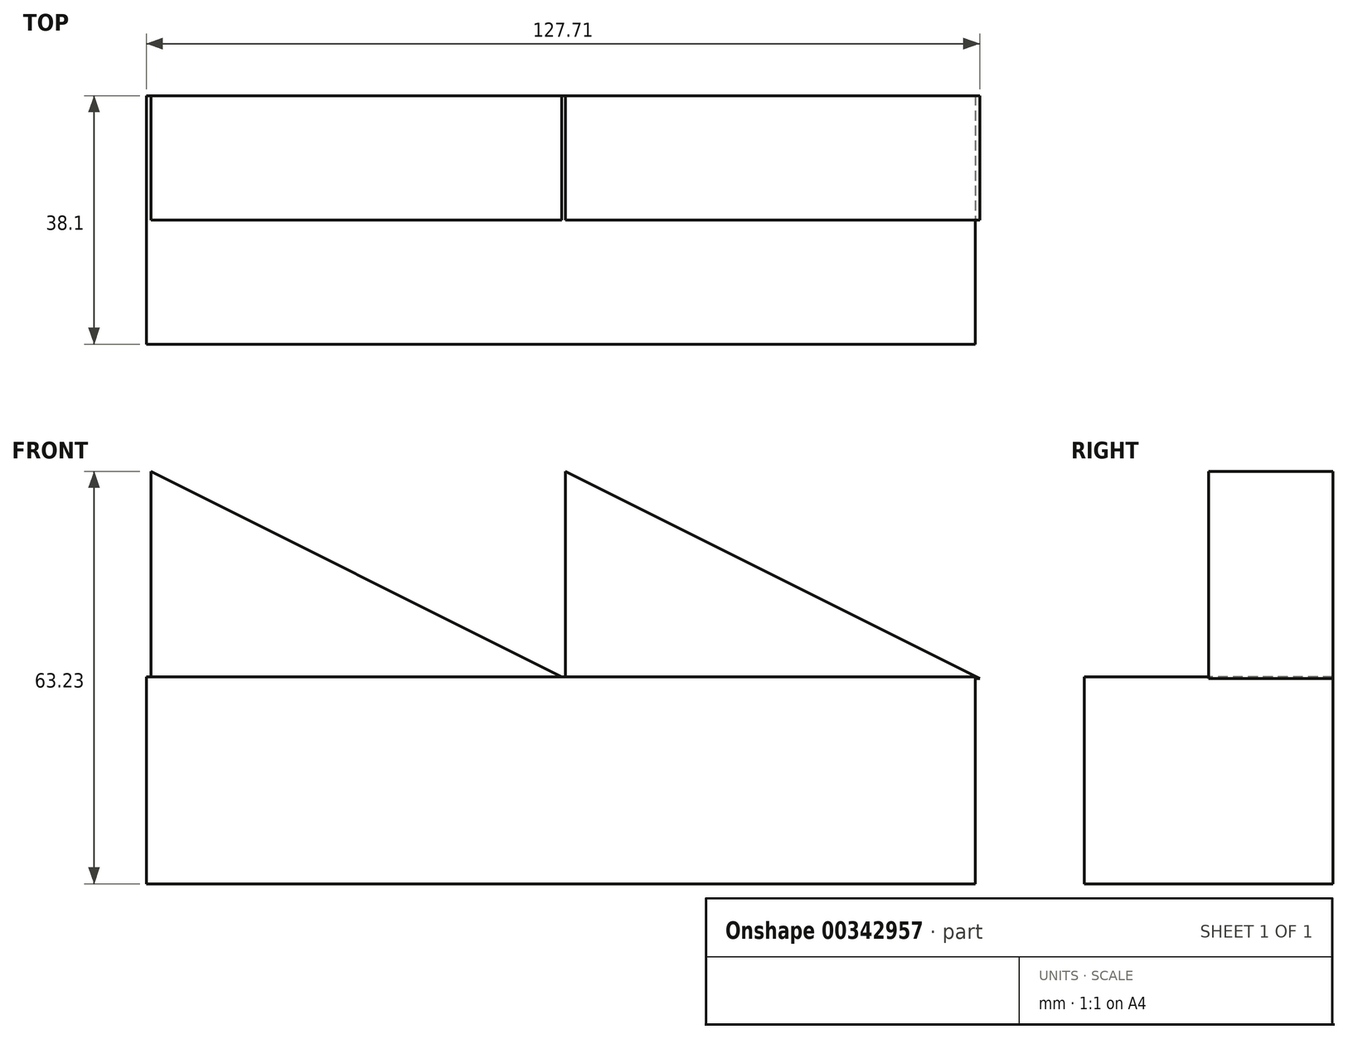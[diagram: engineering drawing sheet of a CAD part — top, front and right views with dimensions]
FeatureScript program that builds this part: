
annotation { "Feature Type Name" : "Feature", "Feature Type Description" : "" }
export const myFeature = defineFeature(function(context is Context, id is Id, definition is map)
    precondition{}
    {
        {
            var Q0;
            Q0=qCreatedBy(makeId("Front.planeOp"),FACE);
            var sketch = newSketch(context, id + "F0", { "sketchPlane" : qUnion([Q0])});
            skLineSegment(sketch, "E0", {"start": v(-53.15, -40.08) * mm, "end": v(73.85, -40.08) * mm});
            skLineSegment(sketch, "E1", {"start": v(-53.15, -40.08) * mm, "end": v(-53.15, -8.33) * mm});
            skLineSegment(sketch, "E2", {"start": v(-53.15, -8.33) * mm, "end": v(73.85, -8.33) * mm});
            skLineSegment(sketch, "E3", {"start": v(73.85, -8.33) * mm, "end": v(73.85, -40.08) * mm});
            skSolve(sketch);
        }
        {
            var Q0;
            Q0=makeQuery(id+"F0.imprint","IMPRINT",FACE,{"disambiguationData":[TD([[makeQuery(id+"F0.imprint","IMPRINT",EDGE,{"derivedFrom":sQuery(id+"F0.wireOp",EDGE,"E0")}),1.0]])]});
            extrude(context, id + "F1", {"entities" : qUnion([Q0]), "depth" : 38.1 * mm});
        }
        {
            var Q0;
            Q0=qCreatedBy(makeId("Front.planeOp"),FACE);
            var sketch = newSketch(context, id + "F2", { "sketchPlane" : qUnion([Q0])});
            skLineSegment(sketch, "E4", {"start": v(-52.44, -8.6) * mm, "end": v(11.06, -8.6) * mm});
            skLineSegment(sketch, "E5", {"start": v(-52.44, -8.6) * mm, "end": v(-52.44, 23.15) * mm});
            skLineSegment(sketch, "E6", {"start": v(-52.44, 23.15) * mm, "end": v(11.06, -8.6) * mm});
            skLineSegment(sketch, "E7", {"start": v(11.06, -8.6) * mm, "end": v(11.06, 23.15) * mm});
            skLineSegment(sketch, "E8", {"start": v(11.06, -8.6) * mm, "end": v(74.56, -8.6) * mm});
            skLineSegment(sketch, "E9", {"start": v(74.56, -8.6) * mm, "end": v(11.06, 23.15) * mm});
            skSolve(sketch);
        }
        {
            var Q0;
            Q0 = qSketchRegion(id + "F2", true);
            extrude(context, id + "F3", {"entities" : qUnion([Q0]), "operationType" : NewBodyOperationType.ADD, "depth" : 19.05 * mm});
        }
    });
